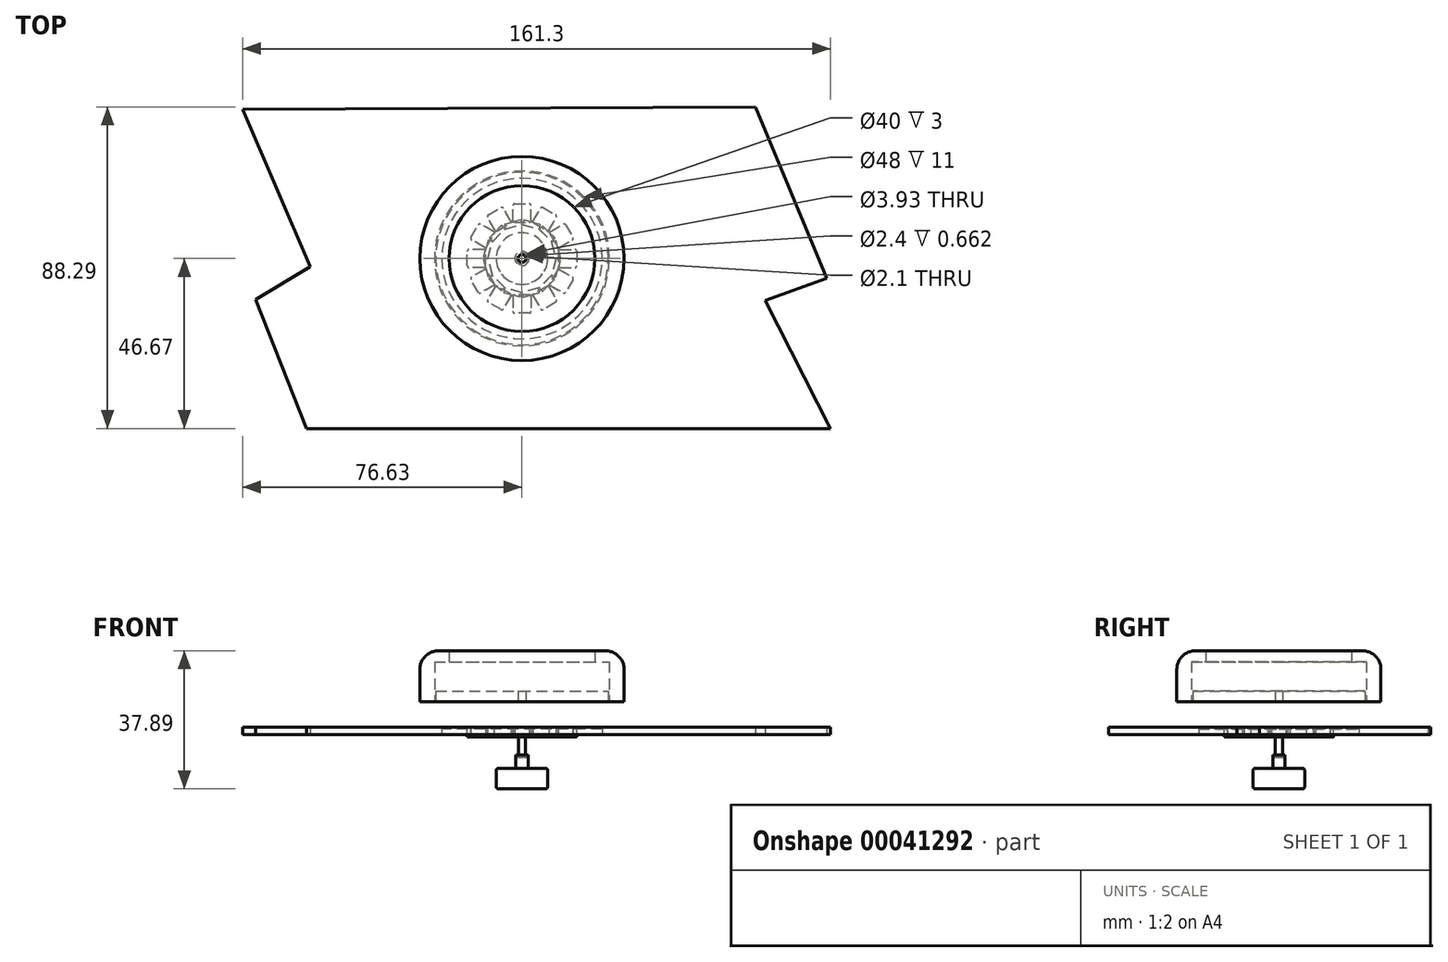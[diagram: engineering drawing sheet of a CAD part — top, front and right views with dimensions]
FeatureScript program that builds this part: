
annotation { "Feature Type Name" : "Feature", "Feature Type Description" : "" }
export const myFeature = defineFeature(function(context is Context, id is Id, definition is map)
    precondition{}
    {
        {
            var Q0;
            Q0=qCreatedBy(makeId("Front.planeOp"),FACE);
            var sketch = newSketch(context, id + "F0", { "sketchPlane" : qUnion([Q0])});
            skLineSegment(sketch, "E0", {"start": v(20, 23) * mm, "end": v(28, 23) * mm});
            skLineSegment(sketch, "E1", {"start": v(28, 23) * mm, "end": v(28, 9) * mm});
            skLineSegment(sketch, "E2", {"start": v(28, 9) * mm, "end": v(24, 9) * mm});
            skLineSegment(sketch, "E3", {"start": v(24, 9) * mm, "end": v(24, 20) * mm});
            skLineSegment(sketch, "E4", {"start": v(24, 20) * mm, "end": v(20, 20) * mm});
            skLineSegment(sketch, "E5", {"start": v(0, 0) * mm, "end": v(0, 20) * mm, "construction": true});
            skLineSegment(sketch, "E6", {"start": v(20, 23) * mm, "end": v(20, 20) * mm});
            skLineSegment(sketch, "E7", {"start": v(0, 20) * mm, "end": v(20, 20) * mm, "construction": true});
            skSolve(sketch);
        }
        {
            var Q0;
            Q0=makeQuery(id+"F0.imprint","IMPRINT",FACE,{"disambiguationData":[TD([[makeQuery(id+"F0.imprint","IMPRINT",EDGE,{"derivedFrom":sQuery(id+"F0.wireOp",EDGE,"E0")}),-1.0]])]});
            var Q1;
            Q1=sQuery(id+"F0.wireOp",EDGE,"E5");
            revolve(context, id + "F1", {"entities" : qUnion([Q0]), "axis" : qUnion([Q1]), "revolveType" : RevolveType.FULL});
        }
        {
            var Q0;
            Q0=makeQuery(id+"F1.opRevolve","SWEPT_EDGE",EDGE,{"disambiguationData":[OSD([sQuery(id+"F0.wireOp",EDGE,"E0"),sQuery(id+"F0.wireOp",EDGE,"E1")])]});
            fillet(context, id + "F2", {"entities" : qUnion([Q0]), "radius" : 5 * mm, "tangentPropagation" : true, "allowEdgeOverflow" : false});
        }
        {
            var Q0;
            Q0=qCreatedBy(makeId("Top.planeOp"),FACE);
            var sketch = newSketch(context, id + "F3", { "sketchPlane" : qUnion([Q0])});
            skCircle(sketch, "E8", {"center": v(0, 0) * mm, "radius": 10 * mm, "construction": true});
            skLineSegment(sketch, "E9.bottom", {"start": v(-2.5, 10) * mm, "end": v(2.5, 10) * mm});
            skLineSegment(sketch, "E9.top", {"start": v(-2.5, 15) * mm, "end": v(2.5, 15) * mm});
            skLineSegment(sketch, "E9.right", {"start": v(2.5, 10) * mm, "end": v(2.5, 15) * mm});
            skLineSegment(sketch, "E10", {"start": v(0, 0) * mm, "end": v(0, 10) * mm, "construction": true});
            skLineSegment(sketch, "E11", {"start": v(-2.5, 10) * mm, "end": v(-2.5, 15) * mm});
            skLineSegment(sketch, "E12", {"start": v(-2.5, 10) * mm, "end": v(-4.86, 9.37) * mm});
            skLineSegment(sketch, "E13", {"start": v(-4.86, 9.37) * mm, "end": v(-4.53, 8.12) * mm});
            skLineSegment(sketch, "E14", {"start": v(-4.53, 8.12) * mm, "end": v(0, 9.32) * mm});
            skLineSegment(sketch, "E15", {"start": v(0, 9.32) * mm, "end": v(4.71, 8.12) * mm});
            skLineSegment(sketch, "E16", {"start": v(4.71, 8.12) * mm, "end": v(5.02, 9.37) * mm});
            skLineSegment(sketch, "E17", {"start": v(5.02, 9.37) * mm, "end": v(2.5, 10) * mm});
            skSolve(sketch);
        }
        {
            var Q0;
            Q0=qSketchRegion(id+"F3",true);
            extrude(context, id + "F4", {"entities" : qUnion([Q0]), "oppositeDirection" : true, "depth" : .6 * mm});
        }
        {
            var Q0;
            Q0=makeQuery(id+"F3.imprint","IMPRINT",FACE,{"disambiguationData":[TD([[makeQuery(id+"F3.imprint","IMPRINT",EDGE,{"derivedFrom":sQuery(id+"F3.wireOp",EDGE,"E9.bottom")}),1.0]])]});
            extrude(context, id + "F5", {"entities" : qUnion([Q0]), "operationType" : NewBodyOperationType.ADD, "depth" : 2 * mm});
        }
        {
            var Q0;
            Q0=makeQuery(id+"F5.opExtrude","SWEPT_EDGE",EDGE,{"disambiguationData":[OSD([sQuery(id+"F3.wireOp",EDGE,"E9.bottom"),sQuery(id+"F3.wireOp",EDGE,"E9.right"),sQuery(id+"F3.wireOp",EDGE,"E17")])]});
            var Q1;
            {var subQ0=sQuery(id+"F3.wireOp",EDGE,"E9.top");var subQ1=sQuery(id+"F3.wireOp",EDGE,"E9.right");Q1=makeQuery(id+"F5.boolean.opBoolean","MERGE",EDGE,{"derivedFrom":[makeQuery(id+"F4.opExtrude","SWEPT_EDGE",EDGE,{"disambiguationData":[OSD([subQ0,subQ1])]}),makeQuery(id+"F5.opExtrude","SWEPT_EDGE",EDGE,{"disambiguationData":[OSD([subQ0,subQ1])]})]});}
            var Q2;
            Q2=makeQuery(id+"F5.opExtrude","SWEPT_EDGE",EDGE,{"disambiguationData":[OSD([sQuery(id+"F3.wireOp",EDGE,"E9.bottom"),sQuery(id+"F3.wireOp",EDGE,"E11"),sQuery(id+"F3.wireOp",EDGE,"E12")])]});
            var Q3;
            {var subQ0=sQuery(id+"F3.wireOp",EDGE,"E9.top");var subQ1=sQuery(id+"F3.wireOp",EDGE,"E11");Q3=makeQuery(id+"F5.boolean.opBoolean","MERGE",EDGE,{"derivedFrom":[makeQuery(id+"F4.opExtrude","SWEPT_EDGE",EDGE,{"disambiguationData":[OSD([subQ0,subQ1])]}),makeQuery(id+"F5.opExtrude","SWEPT_EDGE",EDGE,{"disambiguationData":[OSD([subQ0,subQ1])]})]});}
            fillet(context, id + "F6", {"entities" : qUnion([Q0, Q1, Q2, Q3]), "radius" : .5 * mm, "tangentPropagation" : true, "allowEdgeOverflow" : false});
        }
        {
            var Q0;
            Q0=makeQuery(id+"F4.opExtrude","SWEPT_BODY",BODY,{"disambiguationData":[OSD([sQuery(id+"F3.wireOp",EDGE,"E9.top"),sQuery(id+"F3.wireOp",EDGE,"E9.right"),sQuery(id+"F3.wireOp",EDGE,"E11"),sQuery(id+"F3.wireOp",EDGE,"E12"),sQuery(id+"F3.wireOp",EDGE,"E13"),sQuery(id+"F3.wireOp",EDGE,"E14"),sQuery(id+"F3.wireOp",EDGE,"E15"),sQuery(id+"F3.wireOp",EDGE,"E16"),sQuery(id+"F3.wireOp",EDGE,"E17")])]});
            var Q1;
            Q1=sQuery(id+"F0.wireOp",EDGE,"E5");
            circularPattern(context, id + "F7", {"operationType" : NewBodyOperationType.ADD, "entities" : qUnion([Q0]), "axis" : qUnion([Q1]), "angle" : 360 * degree, "instanceCount" : round(12), "equalSpace" : true});
        }
        {
            var Q0;
            Q0=qCreatedBy(makeId("Top.planeOp"),FACE);
            var sketch = newSketch(context, id + "F8", { "sketchPlane" : qUnion([Q0])});
            skCircle(sketch, "E18", {"center": v(0, 0) * mm, "radius": 22 * mm});
            skSolve(sketch);
        }
        {
            var Q0;
            Q0=qSketchRegion(id+"F8",true);
            extrude(context, id + "F9", {"entities" : qUnion([Q0]), "depth" : 1.5 * mm});
        }
        {
            var Q0;
            Q0=makeQuery(id+"F1.opRevolve","SWEPT_FACE",FACE,{"disambiguationData":[OSD([sQuery(id+"F0.wireOp",EDGE,"E2")])]});
            var sketch = newSketch(context, id + "F10", { "sketchPlane" : qUnion([Q0])});
            skCircle(sketch, "E19", {"center": v(0, 0) * mm, "radius": 23.66 * mm});
            skCircle(sketch, "E20", {"center": v(0, 0) * mm, "radius": 1.05 * mm});
            skSolve(sketch);
        }
        {
            var Q0;
            Q0=qSketchRegion(id+"F10",true);
            extrude(context, id + "F11", {"entities" : qUnion([Q0]), "oppositeDirection" : true, "depth" : 3 * mm});
        }
        {
            var Q0;
            Q0=qCreatedBy(makeId("Front.planeOp"),FACE);
            var sketch = newSketch(context, id + "F12", { "sketchPlane" : qUnion([Q0])});
            skLineSegment(sketch, "E21", {"start": v(0, -14.9) * mm, "end": v(0, 0) * mm});
            skLineSegment(sketch, "E22", {"start": v(0, 0) * mm, "end": v(1, 0) * mm});
            skLineSegment(sketch, "E23", {"start": v(1, 0) * mm, "end": v(1, -6.22) * mm});
            skLineSegment(sketch, "E24", {"start": v(1, -6.22) * mm, "end": v(1.2, -6.22) * mm});
            skLineSegment(sketch, "E25", {"start": v(1.2, -6.22) * mm, "end": v(1.2, -5.56) * mm});
            skLineSegment(sketch, "E26", {"start": v(1.2, -5.56) * mm, "end": v(1.69, -5.56) * mm});
            skLineSegment(sketch, "E27", {"start": v(1.69, -5.56) * mm, "end": v(1.69, -9.2) * mm});
            skLineSegment(sketch, "E28", {"start": v(1.69, -9.2) * mm, "end": v(7.06, -9.2) * mm});
            skLineSegment(sketch, "E29", {"start": v(7.06, -9.2) * mm, "end": v(7.06, -14.9) * mm});
            skLineSegment(sketch, "E30", {"start": v(7.06, -14.9) * mm, "end": v(0, -14.9) * mm});
            skSolve(sketch);
        }
        {
            var Q0;
            Q0=qSketchRegion(id+"F12",true);
            var Q1;
            Q1=sQuery(id+"F12.wireOp",EDGE,"E21");
            revolve(context, id + "F13", {"entities" : qUnion([Q0]), "axis" : qUnion([Q1]), "revolveType" : RevolveType.FULL});
        }
        {
            var Q0;
            Q0=makeQuery(id+"F13.opRevolve","SWEPT_EDGE",EDGE,{"disambiguationData":[OSD([sQuery(id+"F12.wireOp",EDGE,"E28"),sQuery(id+"F12.wireOp",EDGE,"E29")])]});
            var Q1;
            Q1=makeQuery(id+"F13.opRevolve","SWEPT_EDGE",EDGE,{"disambiguationData":[OSD([sQuery(id+"F12.wireOp",EDGE,"E29"),sQuery(id+"F12.wireOp",EDGE,"E30")])]});
            fillet(context, id + "F14", {"entities" : qUnion([Q0, Q1]), "radius" : .6 * mm, "tangentPropagation" : true, "allowEdgeOverflow" : false});
        }
        {
            var Q0;
            Q0=qCreatedBy(makeId("Top.planeOp"),FACE);
            var sketch = newSketch(context, id + "F15", { "sketchPlane" : qUnion([Q0])});
            skLineSegment(sketch, "E31", {"start": v(-76.63, 40.92) * mm, "end": v(64.08, 41.62) * mm});
            skLineSegment(sketch, "E32", {"start": v(64.08, 41.62) * mm, "end": v(83.68, -5.36) * mm});
            skLineSegment(sketch, "E33", {"start": v(83.68, -5.36) * mm, "end": v(66.68, -11.5) * mm});
            skLineSegment(sketch, "E34", {"start": v(66.68, -11.5) * mm, "end": v(84.67, -46.67) * mm});
            skLineSegment(sketch, "E35", {"start": v(84.67, -46.67) * mm, "end": v(-59.15, -46.67) * mm});
            skLineSegment(sketch, "E36", {"start": v(-59.15, -46.67) * mm, "end": v(-73.09, -11.26) * mm});
            skLineSegment(sketch, "E37", {"start": v(-73.09, -11.26) * mm, "end": v(-58.04, -2.2) * mm});
            skLineSegment(sketch, "E38", {"start": v(-58.04, -2.2) * mm, "end": v(-76.63, 40.92) * mm});
            skCircle(sketch, "E39", {"center": v(0, 0) * mm, "radius": 1.97 * mm});
            skSolve(sketch);
        }
        {
            var Q0;
            Q0=qSketchRegion(id+"F15",true);
            extrude(context, id + "F16", {"entities" : qUnion([Q0]), "depth" : 2 * mm});
        }
    });
